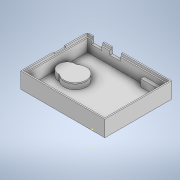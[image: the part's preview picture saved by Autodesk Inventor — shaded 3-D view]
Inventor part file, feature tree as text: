
AUTODESK INVENTOR PART (.ipt)
format: ipt  version: 2022 (Build 260153000, 153)  size: 281,088 bytes
history: native  units: in
note: dims shown in document units (in); Inventor stores cm internally (conversion verified against a paired STEP export)
features: sketch x10, extrude x10, fillet x1
ambient origin geometry x8: Origin, YZ Plane, XZ Plane, XY Plane, X Axis, Y Axis, Z Axis, Center Point
bodies: Solid1 (feature_tree)
feature tree (21):
  sketch  "Sketch1"  dims[d2=0.5118in d3=0.0in d6=0.0787in]
  extrude  "Extrusion1"  Depth=0.0787in
  sketch  "Sketch3"  dims[d8=0.0787in d13=0.4724in d14=0.0in]
  extrude  "Extrusion2"  Depth=0.4724in TaperAngle=0.0deg
  extrude  "Extrusion5"  Depth=0.5906in
  extrude  "Extrusion7"  Depth=0.2362in TaperAngle=0.0deg
  extrude  "Extrusion8"  Depth=0.0787in TaperAngle=0.0deg
  extrude  "Extrusion9"  Depth=0.0394in
  extrude  "Extrusion10"  Depth=0.0787in
  fillet  "Fillet8"  Radius=0.0787in
  extrude  "Extrusion11"  Depth=0.315in
  extrude  "Extrusion12"  Depth=0.3346in
  extrude  "Extrusion13"  Depth=1.126in
  sketch  "Sketch4"  dims[d55=0.1181in d56=0.5906in]
  sketch  "Sketch10"  dims[d60=0.5906in d64=0.2362in d65=0.0in]
  sketch  "Sketch12"  dims[d79=0.2362in d80=0.0in d88=0.0787in d89=0.0in]
  sketch  "Sketch15"  dims[d94=0.0394in d95=0.0394in d96=0.0394in d97=0.0394in d99=0.0394in]
  sketch  "Sketch16"  dims[d101=0.0394in d102=0.0787in d104=0.0787in]
  sketch  "Sketch17"  dims[d108=0.1181in d118=0.315in]
  sketch  "Sketch18"  dims[d125=0.3937in d126=0.0in d127=0.3346in]
  sketch  "Sketch19"  dims[d128=0.3346in d131=1.126in d132=0.5315in d133=0.3937in d134=0.0in d140=1.0933in d141=0.3543in d143=0.1969in d145=0.1181in d148=0.1969in d149=0.2362in d150=0.1575in d151=2.6772in d152=2.126in d153=0.0787in d154=0.0787in d155=0.0in d158=0.315in d159=0.2559in d160=0.1575in d162=0.1969in d163=0.0in d165=0.0394in d166=0.0394in d167=0.1969in d168=0.0in d169=0.0394in d170=0.0in d40=0.0197in d41=0.0344in d42=0.0197in d43=0.0344in d66=0.0197in d67=0.0344in d74=0.0197in d75=0.0344in d76=0.0197in d77=0.0344in d115=0.0in d116=0.0in d117=0.0in d135=0.0197in d136=0.0344in d137=0.0197in d138=0.0344in d171=0.0197in d172=0.0344in d173=0.0197in d174=0.0344in]
